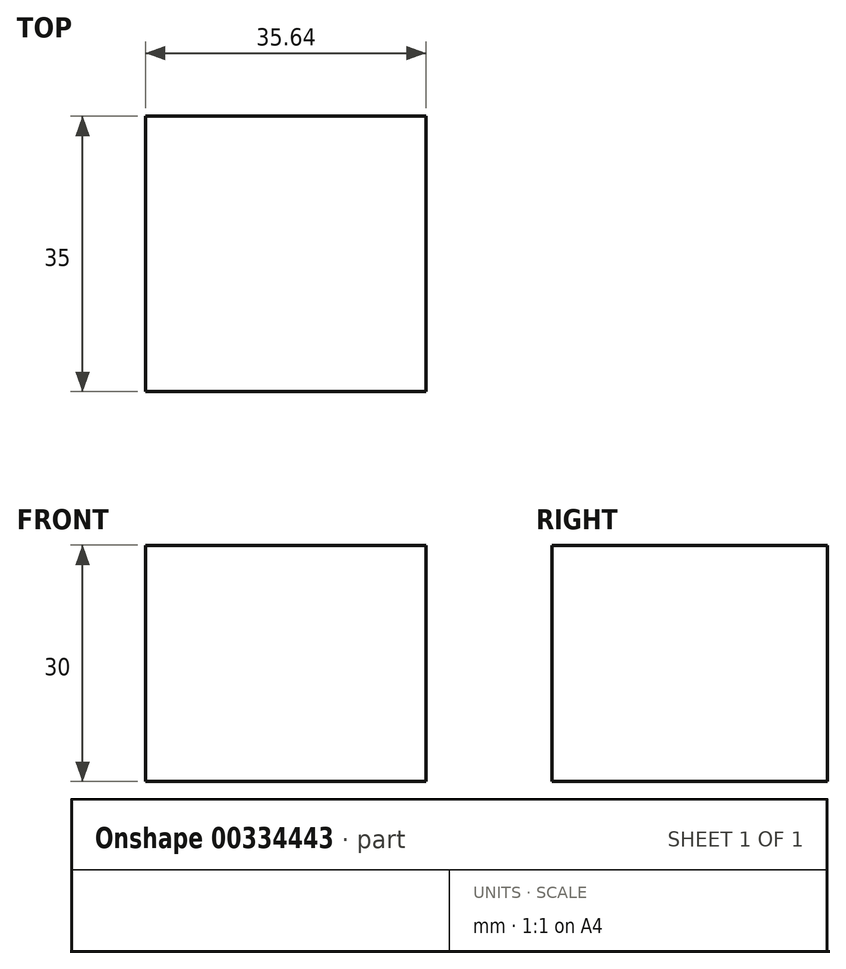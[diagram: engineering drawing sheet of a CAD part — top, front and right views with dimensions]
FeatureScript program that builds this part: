
annotation { "Feature Type Name" : "Feature", "Feature Type Description" : "" }
export const myFeature = defineFeature(function(context is Context, id is Id, definition is map)
    precondition{}
    {
        {
            var Q0;
            Q0=qCreatedBy(makeId("Front.planeOp"),FACE);
            var sketch = newSketch(context, id + "F0", { "sketchPlane" : qUnion([Q0])});
            skLineSegment(sketch, "E0.bottom", {"start": v(-16.54, 13.83) * mm, "end": v(19.1, 13.83) * mm});
            skLineSegment(sketch, "E0.top", {"start": v(-16.54, -16.17) * mm, "end": v(19.1, -16.17) * mm});
            skLineSegment(sketch, "E0.left", {"start": v(-16.54, 13.83) * mm, "end": v(-16.54, -16.17) * mm});
            skLineSegment(sketch, "E0.right", {"start": v(19.1, 13.83) * mm, "end": v(19.1, -16.17) * mm});
            skSolve(sketch);
        }
        {
            var Q0;
            Q0 = qSketchRegion(id + "F0", true);
            extrude(context, id + "F1", {"entities" : qUnion([Q0]), "oppositeDirection" : true, "depth" : 35 * mm});
        }
    });
